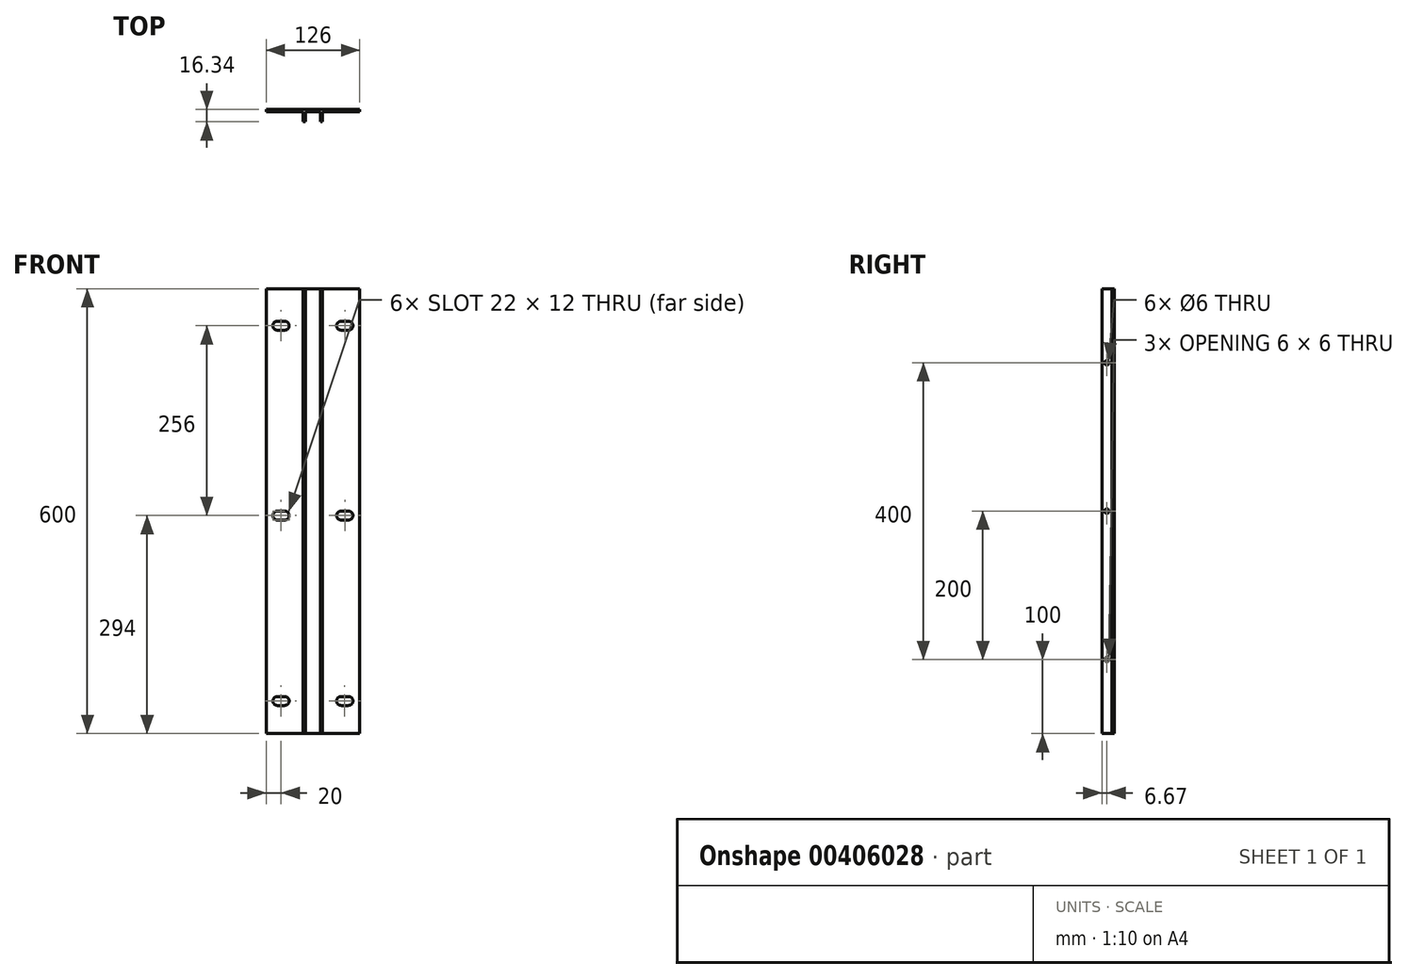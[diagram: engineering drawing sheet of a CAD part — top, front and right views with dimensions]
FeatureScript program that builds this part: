
annotation { "Feature Type Name" : "Feature", "Feature Type Description" : "" }
export const myFeature = defineFeature(function(context is Context, id is Id, definition is map)
    precondition{}
    {
        {
            var Q0;
            Q0=qCreatedBy(makeId("Top.planeOp"),FACE);
            var sketch = newSketch(context, id + "F0", { "sketchPlane" : qUnion([Q0])});
            skLineSegment(sketch, "E0", {"start": v(-63, 0) * mm, "end": v(63, 0) * mm});
            skLineSegment(sketch, "E1", {"start": v(63, 0) * mm, "end": v(63, -3) * mm});
            skLineSegment(sketch, "E2", {"start": v(63, -3) * mm, "end": v(13, -3) * mm});
            skLineSegment(sketch, "E3", {"start": v(13, -3) * mm, "end": v(13, -16.34) * mm});
            skLineSegment(sketch, "E4", {"start": v(13, -16.34) * mm, "end": v(10, -16.34) * mm});
            skLineSegment(sketch, "E5", {"start": v(10, -16.34) * mm, "end": v(10, -3) * mm});
            skLineSegment(sketch, "E6", {"start": v(10, -3) * mm, "end": v(-10, -3) * mm});
            skLineSegment(sketch, "E7", {"start": v(-10, -3) * mm, "end": v(-10, -16.34) * mm});
            skLineSegment(sketch, "E8", {"start": v(-10, -16.34) * mm, "end": v(-13, -16.34) * mm});
            skLineSegment(sketch, "E9", {"start": v(-13, -16.34) * mm, "end": v(-13, -3) * mm});
            skLineSegment(sketch, "E10", {"start": v(-13, -3) * mm, "end": v(-63, -3) * mm});
            skLineSegment(sketch, "E11", {"start": v(-63, -3) * mm, "end": v(-63, 0) * mm});
            skSolve(sketch);
        }
        {
            var Q0;
            Q0 = qSketchRegion(id + "F0", true);
            extrude(context, id + "F1", {"entities" : qUnion([Q0]), "depth" : 600 * mm});
        }
        {
            var Q0;
            Q0=makeQuery(id+"F1.opExtrude","SWEPT_FACE",FACE,{"disambiguationData":[OSD([sQuery(id+"F0.wireOp",EDGE,"E10")])]});
            var sketch = newSketch(context, id + "F2", { "sketchPlane" : qUnion([Q0])});
            skLineSegment(sketch, "E12", {"start": v(-63, 600) * mm, "end": v(-48, 600) * mm, "construction": true});
            skLineSegment(sketch, "E13", {"start": v(-48, 600) * mm, "end": v(-38, 600) * mm, "construction": true});
            skLineSegment(sketch, "E14", {"start": v(-48, 600) * mm, "end": v(-48, 0) * mm, "construction": true});
            skLineSegment(sketch, "E15", {"start": v(-38, 600) * mm, "end": v(-38, 0) * mm, "construction": true});
            skLineSegment(sketch, "E16", {"start": v(-48, 556) * mm, "end": v(-38, 556) * mm});
            skLineSegment(sketch, "E17", {"start": v(-48, 556) * mm, "end": v(-48, 544) * mm, "construction": true});
            skLineSegment(sketch, "E18", {"start": v(-48, 544) * mm, "end": v(-38, 544) * mm});
            skArc(sketch, "E19", {"start": v(-48, 556) * mm, "mid": v(-54, 550) * mm, "end": v(-48, 544) * mm});
            skArc(sketch, "E20", {"start": v(-38, 544) * mm, "mid": v(-32, 550) * mm, "end": v(-38, 556) * mm});
            skLineSegment(sketch, "E21", {"start": v(-48, 550) * mm, "end": v(-38, 550) * mm, "construction": true});
            skLineSegment(sketch, "E22", {"start": v(-43, 550) * mm, "end": v(-43, 300) * mm, "construction": true});
            skLineSegment(sketch, "E23", {"start": v(-48, 300) * mm, "end": v(-38, 300) * mm});
            skLineSegment(sketch, "E24", {"start": v(-48, 288) * mm, "end": v(-38, 288) * mm});
            skArc(sketch, "E25", {"start": v(-48, 300) * mm, "mid": v(-54, 294) * mm, "end": v(-48, 288) * mm});
            skArc(sketch, "E26", {"start": v(-38, 288) * mm, "mid": v(-32, 294) * mm, "end": v(-38, 300) * mm});
            skLineSegment(sketch, "E27", {"start": v(-47.93, 50) * mm, "end": v(-37.93, 50) * mm});
            skLineSegment(sketch, "E28", {"start": v(-47.93, 38) * mm, "end": v(-37.93, 38) * mm});
            skArc(sketch, "E29", {"start": v(-47.93, 50) * mm, "mid": v(-53.93, 44) * mm, "end": v(-47.93, 38) * mm});
            skArc(sketch, "E30", {"start": v(-37.93, 38) * mm, "mid": v(-31.93, 44) * mm, "end": v(-37.93, 50) * mm});
            skLineSegment(sketch, "E31", {"start": v(0, 599.64) * mm, "end": v(0, 142.83) * mm, "construction": true});
            skLineSegment(sketch, "E32", {"start": v(0, 142.83) * mm, "end": v(0, 0) * mm, "construction": true});
            skLineSegment(sketch, "E33.MirrorCS", {"start": v(47.93, 50) * mm, "end": v(37.93, 50) * mm});
            skLineSegment(sketch, "E34.MirrorCS", {"start": v(48, 300) * mm, "end": v(38, 300) * mm});
            skArc(sketch, "E35.MirrorCS", {"start": v(37.93, 38) * mm, "mid": v(31.93, 44) * mm, "end": v(37.93, 50) * mm});
            skArc(sketch, "E36.MirrorCS", {"start": v(47.93, 50) * mm, "mid": v(53.93, 44) * mm, "end": v(47.93, 38) * mm});
            skArc(sketch, "E37.MirrorCS", {"start": v(38, 544) * mm, "mid": v(32, 550) * mm, "end": v(38, 556) * mm});
            skArc(sketch, "E38.MirrorCS", {"start": v(38, 288) * mm, "mid": v(32, 294) * mm, "end": v(38, 300) * mm});
            skLineSegment(sketch, "E39.MirrorCS", {"start": v(47.93, 38) * mm, "end": v(37.93, 38) * mm});
            skLineSegment(sketch, "E40.MirrorCS", {"start": v(48, 288) * mm, "end": v(38, 288) * mm});
            skLineSegment(sketch, "E41.MirrorCS", {"start": v(48, 556) * mm, "end": v(38, 556) * mm});
            skArc(sketch, "E42.MirrorCS", {"start": v(48, 556) * mm, "mid": v(54, 550) * mm, "end": v(48, 544) * mm});
            skArc(sketch, "E43.MirrorCS", {"start": v(48, 300) * mm, "mid": v(54, 294) * mm, "end": v(48, 288) * mm});
            skLineSegment(sketch, "E44.MirrorCS", {"start": v(48, 544) * mm, "end": v(38, 544) * mm});
            skSolve(sketch);
        }
        {
            var Q0;
            Q0 = qSketchRegion(id + "F2", true);
            extrude(context, id + "F3", {"entities" : qUnion([Q0]), "operationType" : NewBodyOperationType.REMOVE, "endBound" : BoundingType.THROUGH_ALL, "oppositeDirection" : true, "depth" : 25 * mm});
        }
        {
            var Q0;
            Q0=makeQuery(id+"F1.opExtrude","SWEPT_FACE",FACE,{"disambiguationData":[OSD([sQuery(id+"F0.wireOp",EDGE,"E9")])]});
            var sketch = newSketch(context, id + "F4", { "sketchPlane" : qUnion([Q0])});
            skLineSegment(sketch, "E45", {"start": v(9.67, 600) * mm, "end": v(9.67, 0) * mm, "construction": true});
            skCircle(sketch, "E46", {"center": v(9.67, 500) * mm, "radius": 3 * mm});
            skCircle(sketch, "E47", {"center": v(9.67, 300) * mm, "radius": 3 * mm});
            skCircle(sketch, "E48", {"center": v(9.67, 100) * mm, "radius": 3 * mm});
            skSolve(sketch);
        }
        {
            var Q0;
            Q0 = qSketchRegion(id + "F4", true);
            extrude(context, id + "F5", {"entities" : qUnion([Q0]), "operationType" : NewBodyOperationType.REMOVE, "endBound" : BoundingType.THROUGH_ALL, "oppositeDirection" : true, "depth" : 25 * mm});
        }
    });
